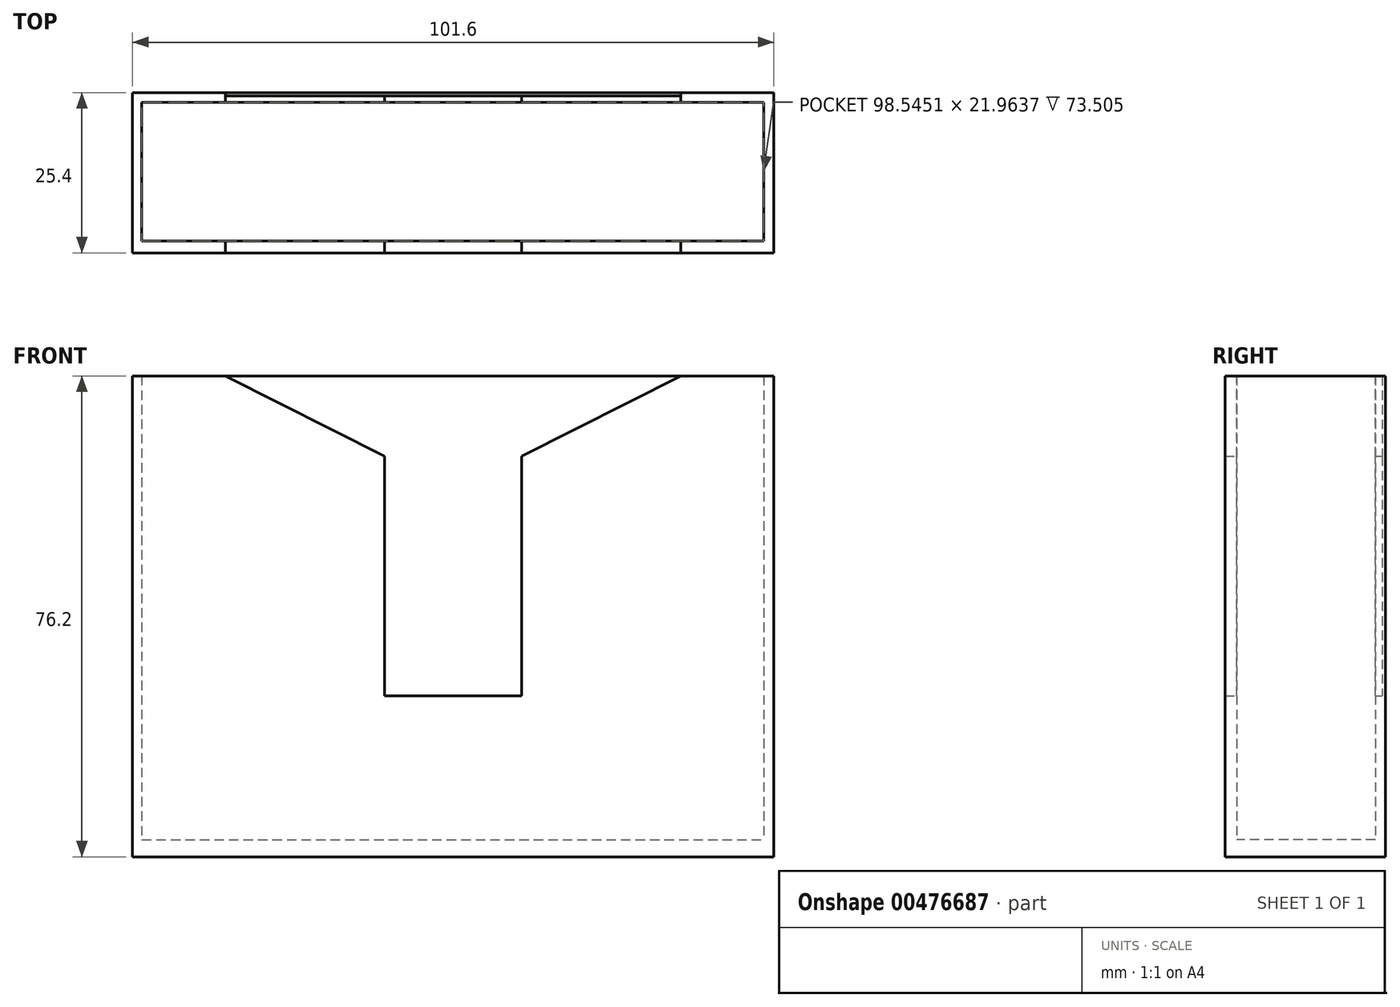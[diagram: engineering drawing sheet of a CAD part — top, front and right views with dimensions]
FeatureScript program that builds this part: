
annotation { "Feature Type Name" : "Feature", "Feature Type Description" : "" }
export const myFeature = defineFeature(function(context is Context, id is Id, definition is map)
    precondition{}
    {
        {
            var Q0;
            Q0=qCreatedBy(makeId("Front.planeOp"),FACE);
            var sketch = newSketch(context, id + "F0", { "sketchPlane" : qUnion([Q0])});
            skLineSegment(sketch, "E0", {"start": v(-50.8, 43.03) * mm, "end": v(-50.8, -33.17) * mm});
            skLineSegment(sketch, "E1", {"start": v(-50.8, -33.17) * mm, "end": v(0, -33.17) * mm});
            skLineSegment(sketch, "E2", {"start": v(-50.8, 43.03) * mm, "end": v(-36.07, 43.03) * mm});
            skLineSegment(sketch, "E3", {"start": v(-36.07, 43.03) * mm, "end": v(-10.87, 30.28) * mm});
            skLineSegment(sketch, "E4", {"start": v(-10.87, 30.28) * mm, "end": v(-10.87, -7.68) * mm});
            skLineSegment(sketch, "E5", {"start": v(-10.87, -7.68) * mm, "end": v(0, -7.68) * mm});
            skLineSegment(sketch, "E6.MirrorCS", {"start": v(50.8, 43.03) * mm, "end": v(50.8, -33.17) * mm});
            skLineSegment(sketch, "E7.MirrorCS", {"start": v(10.87, 30.28) * mm, "end": v(10.87, -7.68) * mm});
            skLineSegment(sketch, "E8.MirrorCS", {"start": v(36.07, 43.03) * mm, "end": v(10.87, 30.28) * mm});
            skLineSegment(sketch, "E9.MirrorCS", {"start": v(50.8, 43.03) * mm, "end": v(36.07, 43.03) * mm});
            skLineSegment(sketch, "E10.MirrorCS", {"start": v(50.8, -33.17) * mm, "end": v(0, -33.17) * mm});
            skLineSegment(sketch, "E11.MirrorCS", {"start": v(10.87, -7.68) * mm, "end": v(0, -7.68) * mm});
            skSolve(sketch);
        }
        {
            var Q0;
            Q0=makeQuery(id+"F0.imprint","IMPRINT",FACE,{"disambiguationData":[TD([[makeQuery(id+"F0.imprint","IMPRINT",EDGE,{"derivedFrom":sQuery(id+"F0.wireOp",EDGE,"E0")}),1.0]])]});
            extrude(context, id + "F1", {"entities" : qUnion([Q0]), "depth" : 25.4 * mm});
        }
        {
            var Q0;
            Q0=qCreatedBy(makeId("Front.planeOp"),FACE);
            var sketch = newSketch(context, id + "F2", { "sketchPlane" : qUnion([Q0])});
            skLineSegment(sketch, "E12.bottom", {"start": v(-50.78, 43) * mm, "end": v(50.8, 43) * mm});
            skLineSegment(sketch, "E12.top", {"start": v(-50.78, -33.18) * mm, "end": v(50.8, -33.18) * mm});
            skLineSegment(sketch, "E12.left", {"start": v(-50.78, 43) * mm, "end": v(-50.78, -33.18) * mm});
            skLineSegment(sketch, "E12.right", {"start": v(50.8, 43) * mm, "end": v(50.8, -33.18) * mm});
            skSolve(sketch);
        }
        {
            var Q0;
            Q0=makeQuery(id+"F2.imprint","IMPRINT",FACE,{"disambiguationData":[TD([[makeQuery(id+"F2.imprint","IMPRINT",EDGE,{"derivedFrom":sQuery(id+"F2.wireOp",EDGE,"E12.bottom")}),-1.0]])]});
            extrude(context, id + "F3", {"entities" : qUnion([Q0]), "operationType" : NewBodyOperationType.ADD, "depth" : 0.5 * mm});
        }
        {
            var Q0;
            Q0=qCreatedBy(makeId("Top.planeOp"),FACE);
            var sketch = newSketch(context, id + "F4", { "sketchPlane" : qUnion([Q0])});
            skLineSegment(sketch, "E13.bottom", {"start": v(49.27, -1.46) * mm, "end": v(-49.3, -1.46) * mm});
            skLineSegment(sketch, "E13.top", {"start": v(49.27, -23.83) * mm, "end": v(-49.3, -23.83) * mm});
            skLineSegment(sketch, "E13.left", {"start": v(49.27, -1.46) * mm, "end": v(49.27, -23.83) * mm});
            skLineSegment(sketch, "E13.right", {"start": v(-49.3, -1.46) * mm, "end": v(-49.3, -23.83) * mm});
            skSolve(sketch);
        }
        {
            var Q0;
            Q0=makeQuery(id+"F4.imprint","IMPRINT",FACE,{"disambiguationData":[TD([[makeQuery(id+"F4.imprint","IMPRINT",EDGE,{"derivedFrom":sQuery(id+"F4.wireOp",EDGE,"E13.bottom")}),1.0]])]});
            cPlane(context, id + "F5", {"entities" : qUnion([Q0]), "cplaneType" : CPlaneType.OFFSET, "offset" : 30.48 * mm, "oppositeDirection" : true, "width" : 152.4 * mm, "height" : 152.4 * mm});
        }
        {
            var Q0;
            Q0=qCreatedBy(id+"F5.planeOp",FACE);
            var sketch = newSketch(context, id + "F6", { "sketchPlane" : qUnion([Q0])});
            skLineSegment(sketch, "E14.bottom", {"start": v(-49.32, -1.58) * mm, "end": v(49.22, -1.58) * mm});
            skLineSegment(sketch, "E14.top", {"start": v(-49.32, -23.54) * mm, "end": v(49.22, -23.54) * mm});
            skLineSegment(sketch, "E14.left", {"start": v(-49.32, -1.58) * mm, "end": v(-49.32, -23.54) * mm});
            skLineSegment(sketch, "E14.right", {"start": v(49.22, -1.58) * mm, "end": v(49.22, -23.54) * mm});
            skSolve(sketch);
        }
        {
            var Q0;
            Q0 = qSketchRegion(id + "F6", true);
            extrude(context, id + "F7", {"entities" : qUnion([Q0]), "operationType" : NewBodyOperationType.REMOVE, "depth" : 152.4 * mm});
        }
    });
